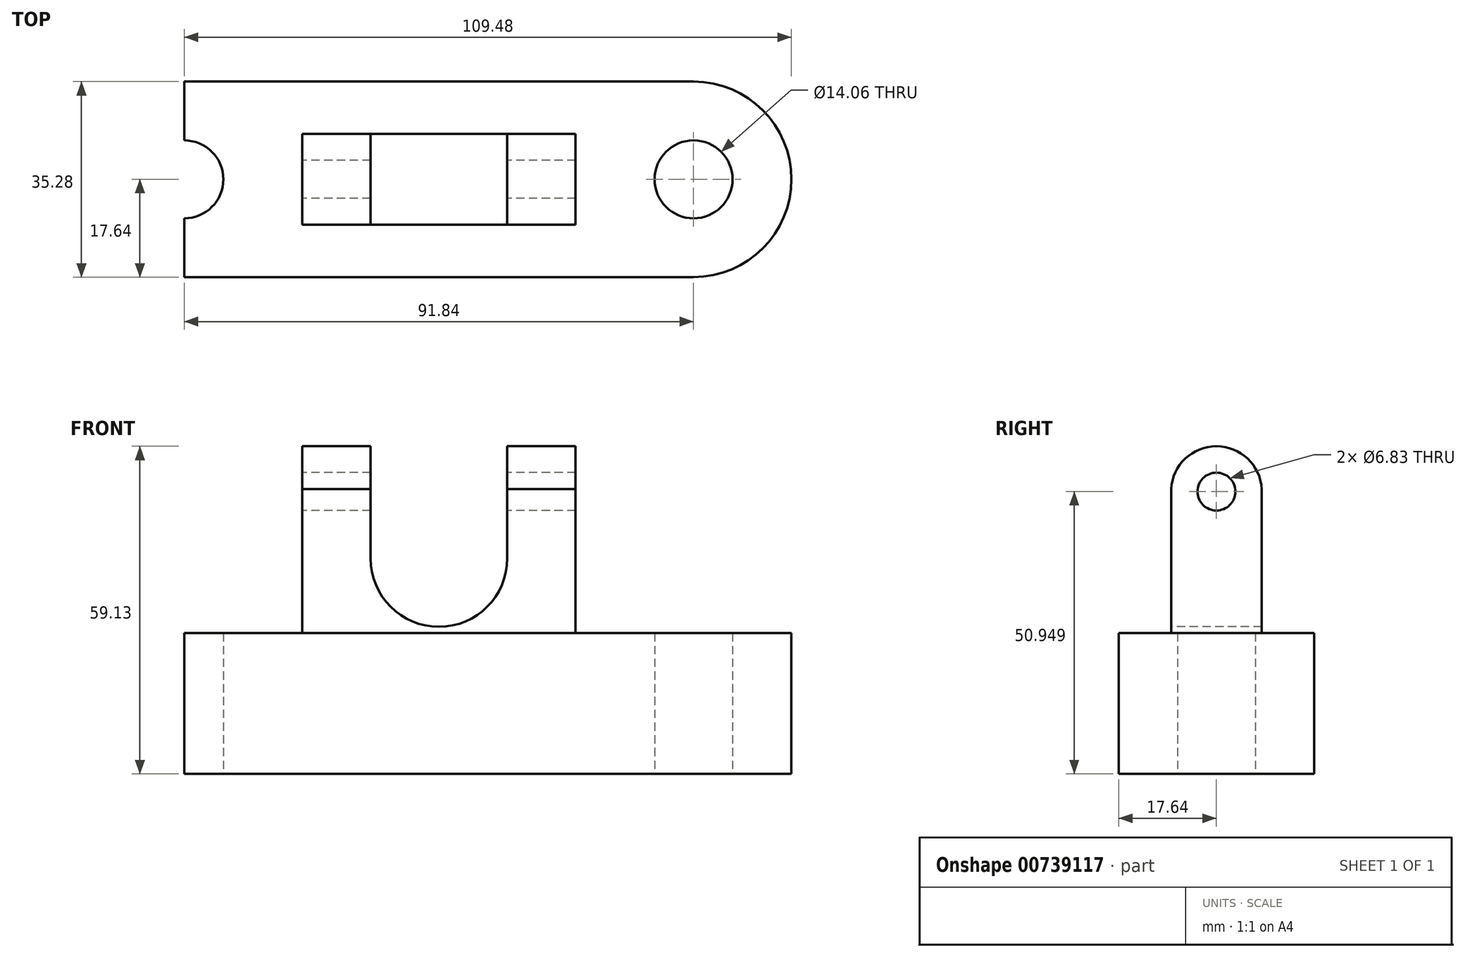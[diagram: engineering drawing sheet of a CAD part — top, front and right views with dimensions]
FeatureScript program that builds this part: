
annotation { "Feature Type Name" : "Feature", "Feature Type Description" : "" }
export const myFeature = defineFeature(function(context is Context, id is Id, definition is map)
    precondition{}
    {
        {
            var Q0;
            Q0=qCreatedBy(makeId("Top.planeOp"),FACE);
            var sketch = newSketch(context, id + "F0", { "sketchPlane" : qUnion([Q0])});
            skLineSegment(sketch, "E0.bottom", {"start": v(45.92, 17.64) * mm, "end": v(-45.92, 17.64) * mm});
            skLineSegment(sketch, "E0.top", {"start": v(45.92, -17.64) * mm, "end": v(-45.92, -17.64) * mm});
            skLineSegment(sketch, "E0.left", {"start": v(45.92, 17.64) * mm, "end": v(45.92, -17.64) * mm});
            skLineSegment(sketch, "E0.right", {"start": v(-45.92, 17.64) * mm, "end": v(-45.92, -17.64) * mm});
            skPoint(sketch, "E0.middle", {"position": v(0, 0) * mm});
            skArc(sketch, "E1", {"start": v(-45.92, -17.64) * mm, "mid": v(-63.56, 0) * mm, "end": v(-45.92, 17.64) * mm});
            skArc(sketch, "E2", {"start": v(45.92, -17.64) * mm, "mid": v(63.56, 0) * mm, "end": v(45.92, 17.64) * mm});
            skCircle(sketch, "E3", {"center": v(-45.92, 0) * mm, "radius": 7.03 * mm});
            skCircle(sketch, "E4", {"center": v(45.92, 0) * mm, "radius": 7.03 * mm});
            skLineSegment(sketch, "E5.bottom", {"start": v(24.63, 8.17) * mm, "end": v(-24.63, 8.17) * mm});
            skLineSegment(sketch, "E5.top", {"start": v(24.63, -8.17) * mm, "end": v(-24.63, -8.17) * mm});
            skLineSegment(sketch, "E5.left", {"start": v(24.63, 8.17) * mm, "end": v(24.63, -8.17) * mm});
            skLineSegment(sketch, "E5.right", {"start": v(-24.63, 8.17) * mm, "end": v(-24.63, -8.17) * mm});
            skSolve(sketch);
        }
        {
            var Q0;
            {var subQ5=sQuery(id+"F0.wireOp",EDGE,"E0.bottom");Q0=makeQuery(id+"F0.imprint","IMPRINT",FACE,{"disambiguationData":[TD([[makeQuery(id+"F0.imprint","IMPRINT",EDGE,{"derivedFrom":subQ5}),1.0]])]});}
            var Q1;
            {var subQ0=sQuery(id+"F0.wireOp",EDGE,"E2");Q1=makeQuery(id+"F0.imprint","IMPRINT",FACE,{"disambiguationData":[TD([[makeQuery(id+"F0.imprint","IMPRINT",EDGE,{"derivedFrom":subQ0}),1.0]])]});}
            var Q2;
            {var subQ0=sQuery(id+"F0.wireOp",EDGE,"E1");Q2=makeQuery(id+"F0.imprint","IMPRINT",FACE,{"disambiguationData":[TD([[makeQuery(id+"F0.imprint","IMPRINT",EDGE,{"derivedFrom":subQ0}),-1.0]])]});}
            extrude(context, id + "F1", {"entities" : qUnion([Q0, Q1, Q2]), "depth" : 25.4 * mm, "offsetDistance" : 25.4 * mm});
        }
        {
            var Q0;
            Q0=makeQuery(id+"F0.imprint","IMPRINT",FACE,{"disambiguationData":[TD([[makeQuery(id+"F0.imprint","IMPRINT",EDGE,{"derivedFrom":sQuery(id+"F0.wireOp",EDGE,"E5.bottom")}),1.0]])]});
            extrude(context, id + "F2", {"entities" : qUnion([Q0]), "operationType" : NewBodyOperationType.ADD, "depth" : 43.94 * mm, "offsetDistance" : 25.4 * mm});
        }
        {
            var Q0;
            Q0=makeQuery(id+"F2.opExtrude","SWEPT_FACE",FACE,{"disambiguationData":[OSD([sQuery(id+"F0.wireOp",EDGE,"E5.top")])]});
            var sketch = newSketch(context, id + "F3", { "sketchPlane" : qUnion([Q0])});
            skLineSegment(sketch, "E6", {"start": v(-24.63, 43.94) * mm, "end": v(0, 43.94) * mm});
            skLineSegment(sketch, "E7", {"start": v(0, 43.94) * mm, "end": v(24.63, 43.94) * mm});
            skLineSegment(sketch, "E8", {"start": v(-12.31, 43.94) * mm, "end": v(-12.31, 38.86) * mm});
            skLineSegment(sketch, "E9", {"start": v(12.31, 43.94) * mm, "end": v(12.31, 38.86) * mm});
            skArc(sketch, "E10", {"start": v(12.31, 38.86) * mm, "mid": v(0, 26.55) * mm, "end": v(-12.31, 38.86) * mm});
            skSolve(sketch);
        }
        {
            var Q0;
            Q0 = qSketchRegion(id + "F3", true);
            extrude(context, id + "F4", {"entities" : qUnion([Q0]), "operationType" : NewBodyOperationType.REMOVE, "oppositeDirection" : true, "depth" : 25.4 * mm, "offsetDistance" : 25.4 * mm});
        }
        {
            var Q0;
            {var subQ0=sQuery(id+"F0.wireOp",EDGE,"E5.bottom");var subQ1=sQuery(id+"F0.wireOp",EDGE,"E5.right");var subQ2=sQuery(id+"F0.wireOp",EDGE,"E5.top");Q0=makeQuery(id+"F4.boolean.opBoolean","SPLIT",FACE,{"disambiguationData":[TD([makeQuery(id+"F2.opExtrude","SWEPT_FACE",FACE,{"disambiguationData":[OSD([subQ1])]})])],"derivedFrom":makeQuery(id+"F2.opExtrude","CAP_FACE",FACE,{"disambiguationData":[OSD([subQ0,subQ2,sQuery(id+"F0.wireOp",EDGE,"E5.left"),subQ1])],"isStart":false})});}
            var Q1;
            {var subQ0=sQuery(id+"F0.wireOp",EDGE,"E5.bottom");var subQ1=sQuery(id+"F0.wireOp",EDGE,"E5.top");var subQ2=sQuery(id+"F0.wireOp",EDGE,"E5.left");Q1=makeQuery(id+"F4.boolean.opBoolean","SPLIT",FACE,{"disambiguationData":[TD([makeQuery(id+"F2.opExtrude","SWEPT_FACE",FACE,{"disambiguationData":[OSD([subQ2])]})])],"derivedFrom":makeQuery(id+"F2.opExtrude","CAP_FACE",FACE,{"disambiguationData":[OSD([subQ0,subQ1,subQ2,sQuery(id+"F0.wireOp",EDGE,"E5.right")])],"isStart":false})});}
            extrude(context, id + "F5", {"entities" : qUnion([Q0, Q1]), "operationType" : NewBodyOperationType.ADD, "depth" : 16.5 * mm, "offsetDistance" : 25.4 * mm});
        }
        {
            var Q0;
            {var subQ0=sQuery(id+"F0.wireOp",EDGE,"E5.right");Q0=makeQuery(id+"F5.boolean.opBoolean","MERGE",FACE,{"derivedFrom":[makeQuery(id+"F2.opExtrude","SWEPT_FACE",FACE,{"disambiguationData":[OSD([subQ0])]}),makeQuery(id+"F5.opExtrude","SWEPT_FACE",FACE,{"disambiguationData":[OSD([subQ0])]})]});}
            var sketch = newSketch(context, id + "F6", { "sketchPlane" : qUnion([Q0])});
            skArc(sketch, "E11", {"start": v(8.17, 51.39) * mm, "mid": v(0, 59.13) * mm, "end": v(-8.17, 51.39) * mm});
            skLineSegment(sketch, "E12", {"start": v(-8.17, 51.39) * mm, "end": v(8.17, 51.39) * mm});
            skSolve(sketch);
        }
        {
            var Q0;
            {var subQ0=sQuery(id+"F6.wireOp",EDGE,"E11");Q0=makeQuery(id+"F6.imprint","IMPRINT",FACE,{"disambiguationData":[TD([[makeQuery(id+"F6.imprint","IMPRINT",EDGE,{"derivedFrom":subQ0}),-1.0]])]});}
            extrude(context, id + "F7", {"entities" : qUnion([Q0]), "operationType" : NewBodyOperationType.REMOVE, "oppositeDirection" : true, "depth" : 78.49 * mm, "offsetDistance" : 25.4 * mm});
        }
        {
            var Q0;
            {var subQ0=sQuery(id+"F0.wireOp",EDGE,"E5.right");Q0=makeQuery(id+"F5.boolean.opBoolean","MERGE",FACE,{"derivedFrom":[makeQuery(id+"F2.opExtrude","SWEPT_FACE",FACE,{"disambiguationData":[OSD([subQ0])]}),makeQuery(id+"F5.opExtrude","SWEPT_FACE",FACE,{"disambiguationData":[OSD([subQ0])]})]});}
            var sketch = newSketch(context, id + "F8", { "sketchPlane" : qUnion([Q0])});
            skCircle(sketch, "E13", {"center": v(0, 50.95) * mm, "radius": 3.41 * mm});
            skSolve(sketch);
        }
        {
            var Q0;
            Q0 = qSketchRegion(id + "F8", true);
            extrude(context, id + "F9", {"entities" : qUnion([Q0]), "operationType" : NewBodyOperationType.REMOVE, "oppositeDirection" : true, "depth" : 57.15 * mm, "offsetDistance" : 25.4 * mm});
        }
    });
